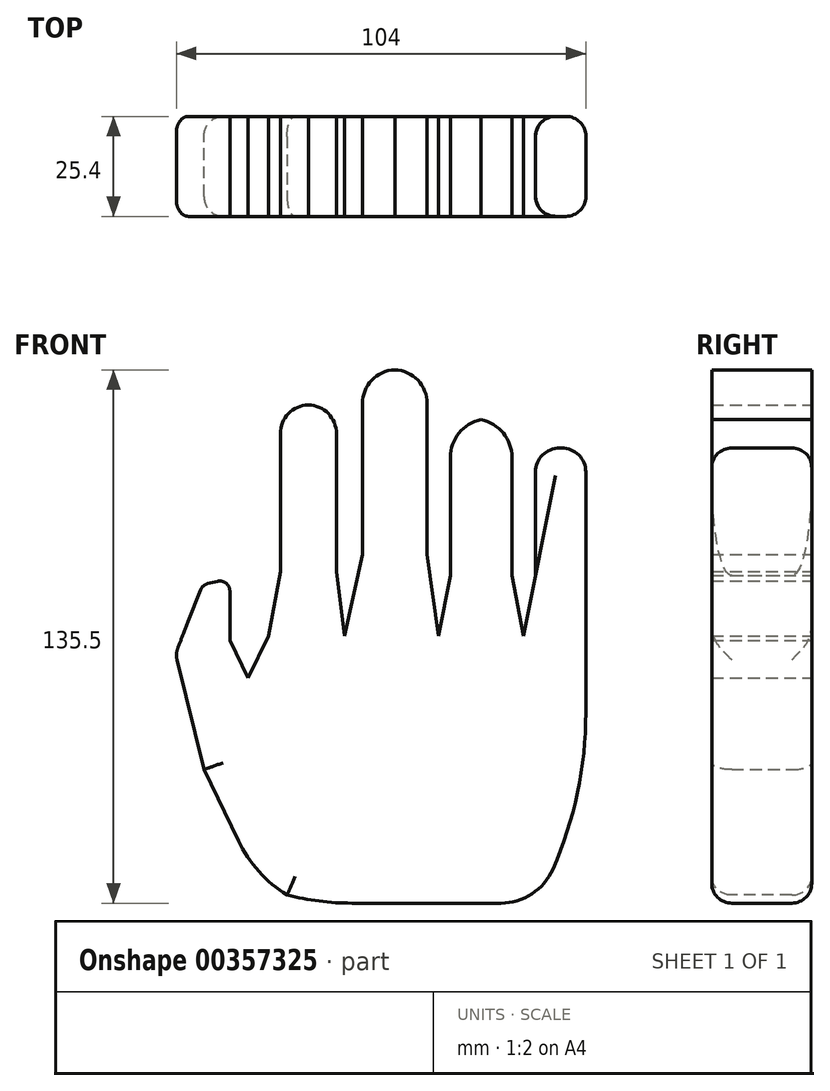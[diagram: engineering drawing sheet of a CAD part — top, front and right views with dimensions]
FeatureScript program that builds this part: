
annotation { "Feature Type Name" : "Feature", "Feature Type Description" : "" }
export const myFeature = defineFeature(function(context is Context, id is Id, definition is map)
    precondition{}
    {
        {
            var Q0;
            Q0=qCreatedBy(makeId("Front.planeOp"),FACE);
            var sketch = newSketch(context, id + "F0", { "sketchPlane" : qUnion([Q0])});
            skLineSegment(sketch, "E0.bottom", {"start": v(-40.3, 33.93) * mm, "end": v(40.3, 33.93) * mm});
            skLineSegment(sketch, "E0.top", {"start": v(-40.3, -33.93) * mm, "end": v(40.3, -33.93) * mm});
            skLineSegment(sketch, "E0.left", {"start": v(-40.3, 33.93) * mm, "end": v(-40.3, -33.93) * mm});
            skLineSegment(sketch, "E0.right", {"start": v(40.3, 33.93) * mm, "end": v(40.3, -33.93) * mm});
            skPoint(sketch, "E0.middle", {"position": v(0, 0) * mm});
            skLineSegment(sketch, "E1", {"start": v(-40.3, -33.93) * mm, "end": v(-56.71, 0) * mm});
            skLineSegment(sketch, "E2", {"start": v(-56.71, 0) * mm, "end": v(-40.3, 33.93) * mm});
            skLineSegment(sketch, "E3", {"start": v(-56.71, 0) * mm, "end": v(-63.94, 29.46) * mm});
            skLineSegment(sketch, "E4", {"start": v(-63.94, 29.46) * mm, "end": v(-50.13, 32.85) * mm});
            skLineSegment(sketch, "E5", {"start": v(-50.13, 32.85) * mm, "end": v(-45.48, 23.23) * mm});
            skLineSegment(sketch, "E6", {"start": v(-40.3, 33.93) * mm, "end": v(-37.32, 50.4) * mm});
            skLineSegment(sketch, "E7", {"start": v(-37.32, 50.4) * mm, "end": v(-23.05, 50.4) * mm});
            skLineSegment(sketch, "E8", {"start": v(-23.05, 50.4) * mm, "end": v(-23.05, 33.93) * mm});
            skLineSegment(sketch, "E9", {"start": v(-23.05, 33.93) * mm, "end": v(-16.47, 33.93) * mm});
            skLineSegment(sketch, "E10", {"start": v(-16.47, 33.93) * mm, "end": v(-16.47, 54.67) * mm});
            skLineSegment(sketch, "E11", {"start": v(-16.47, 54.67) * mm, "end": v(0, 54.67) * mm});
            skLineSegment(sketch, "E12", {"start": v(0, 54.67) * mm, "end": v(0, 33.93) * mm});
            skLineSegment(sketch, "E13", {"start": v(0, 33.93) * mm, "end": v(5.86, 33.93) * mm});
            skLineSegment(sketch, "E14", {"start": v(5.86, 33.93) * mm, "end": v(5.86, 49.26) * mm});
            skLineSegment(sketch, "E15", {"start": v(5.86, 49.26) * mm, "end": v(21.54, 49.26) * mm});
            skLineSegment(sketch, "E16", {"start": v(21.54, 49.26) * mm, "end": v(21.54, 33.93) * mm});
            skLineSegment(sketch, "E17", {"start": v(21.54, 33.93) * mm, "end": v(40.3, 33.93) * mm});
            skLineSegment(sketch, "E18", {"start": v(40.3, 49.26) * mm, "end": v(27.54, 49.26) * mm});
            skLineSegment(sketch, "E19", {"start": v(27.54, 49.26) * mm, "end": v(27.54, 33.93) * mm});
            skLineSegment(sketch, "E20", {"start": v(27.54, 33.93) * mm, "end": v(40.3, 33.93) * mm});
            skLineSegment(sketch, "E21", {"start": v(40.3, 33.93) * mm, "end": v(40.3, 49.26) * mm});
            skLineSegment(sketch, "E22", {"start": v(-37.32, 50.4) * mm, "end": v(-37.32, 70.26) * mm});
            skLineSegment(sketch, "E23", {"start": v(-37.32, 70.26) * mm, "end": v(-23.05, 70.26) * mm});
            skLineSegment(sketch, "E24", {"start": v(-23.05, 70.26) * mm, "end": v(-23.05, 50.4) * mm});
            skLineSegment(sketch, "E25", {"start": v(-16.47, 54.67) * mm, "end": v(-16.47, 76.1) * mm});
            skLineSegment(sketch, "E26", {"start": v(-16.47, 76.1) * mm, "end": v(0, 76.1) * mm});
            skLineSegment(sketch, "E27", {"start": v(0, 76.1) * mm, "end": v(0, 54.67) * mm});
            skLineSegment(sketch, "E28", {"start": v(5.86, 49.26) * mm, "end": v(5.86, 70.26) * mm});
            skLineSegment(sketch, "E29", {"start": v(5.86, 70.26) * mm, "end": v(21.54, 70.26) * mm});
            skLineSegment(sketch, "E30", {"start": v(21.54, 70.26) * mm, "end": v(21.54, 49.26) * mm});
            skLineSegment(sketch, "E31", {"start": v(27.54, 49.26) * mm, "end": v(27.54, 64.67) * mm});
            skLineSegment(sketch, "E32", {"start": v(27.54, 64.67) * mm, "end": v(40.3, 64.67) * mm});
            skLineSegment(sketch, "E33", {"start": v(40.3, 64.67) * mm, "end": v(40.3, 49.26) * mm});
            skLineSegment(sketch, "E34", {"start": v(-37.32, 70.26) * mm, "end": v(-37.32, 92.7) * mm});
            skLineSegment(sketch, "E35", {"start": v(-37.32, 92.7) * mm, "end": v(-23.05, 92.7) * mm});
            skLineSegment(sketch, "E36", {"start": v(-23.05, 92.7) * mm, "end": v(-23.05, 70.26) * mm});
            skLineSegment(sketch, "E37", {"start": v(-16.47, 76.1) * mm, "end": v(-16.47, 101.57) * mm});
            skLineSegment(sketch, "E38", {"start": v(-16.47, 101.57) * mm, "end": v(0, 101.57) * mm});
            skLineSegment(sketch, "E39", {"start": v(0, 101.57) * mm, "end": v(0, 76.1) * mm});
            skLineSegment(sketch, "E40", {"start": v(5.86, 70.26) * mm, "end": v(5.86, 89.12) * mm});
            skLineSegment(sketch, "E41", {"start": v(5.86, 89.12) * mm, "end": v(21.54, 89.12) * mm});
            skLineSegment(sketch, "E42", {"start": v(21.54, 89.12) * mm, "end": v(21.54, 70.26) * mm});
            skLineSegment(sketch, "E43", {"start": v(27.54, 64.67) * mm, "end": v(27.54, 81.74) * mm});
            skLineSegment(sketch, "E44", {"start": v(27.54, 81.74) * mm, "end": v(40.3, 81.74) * mm});
            skLineSegment(sketch, "E45", {"start": v(40.3, 81.74) * mm, "end": v(40.3, 64.67) * mm});
            skLineSegment(sketch, "E46", {"start": v(-63.94, 29.46) * mm, "end": v(-57.03, 46.92) * mm});
            skPoint(sketch, "E46.endSnap0", {"position": v(-57.03, 31.16) * mm});
            skLineSegment(sketch, "E47", {"start": v(-57.03, 46.92) * mm, "end": v(-50.13, 48.6) * mm});
            skLineSegment(sketch, "E48", {"start": v(-50.13, 48.6) * mm, "end": v(-50.13, 32.85) * mm});
            skPoint(sketch, "E49", {"position": v(-40.3, 0) * mm});
            skLineSegment(sketch, "E50", {"start": v(-23.05, 50.4) * mm, "end": v(-20.99, 33.93) * mm});
            skLineSegment(sketch, "E51", {"start": v(-20.99, 33.93) * mm, "end": v(-16.47, 54.67) * mm});
            skLineSegment(sketch, "E52", {"start": v(0, 54.67) * mm, "end": v(2.93, 33.93) * mm});
            skLineSegment(sketch, "E53", {"start": v(2.93, 33.93) * mm, "end": v(5.86, 49.26) * mm});
            skLineSegment(sketch, "E54", {"start": v(21.54, 49.26) * mm, "end": v(24.49, 33.93) * mm});
            skLineSegment(sketch, "E55", {"start": v(24.49, 33.93) * mm, "end": v(27.54, 49.26) * mm});
            skSolve(sketch);
        }
        {
            var Q0;
            Q0 = qSketchRegion(id + "F0", true);
            extrude(context, id + "F1", {"entities" : qUnion([Q0]), "endBound" : BoundingType.SYMMETRIC, "depth" : 25.4 * mm});
        }
        {
            var Q0;
            Q0=makeQuery(id+"F1.opExtrude","SWEPT_EDGE",EDGE,{"disambiguationData":[OSD([sQuery(id+"F0.wireOp",EDGE,"E0.top"),sQuery(id+"F0.wireOp",EDGE,"E0.right")])]});
            var Q1;
            Q1=makeQuery(id+"F1.opExtrude","SWEPT_EDGE",EDGE,{"disambiguationData":[OSD([sQuery(id+"F0.wireOp",EDGE,"E0.top"),sQuery(id+"F0.wireOp",EDGE,"E0.left"),sQuery(id+"F0.wireOp",EDGE,"E1")])]});
            chamfer(context, id + "F2", {"entities" : qUnion([Q0, Q1]), "width" : 12.7 * mm, "tangentPropagation" : true});
        }
        {
            var Q0;
            {var subQ0=sQuery(id+"F0.wireOp",EDGE,"E0.right");Q0=makeQuery(id+"F2.opChamfer","BLEND_EDGE",EDGE,{"blendedFrom":[makeQuery(id+"F1.opExtrude","SWEPT_EDGE",EDGE,{"disambiguationData":[OSD([sQuery(id+"F0.wireOp",EDGE,"E0.top"),subQ0])]}),makeQuery(id+"F1.opExtrude","SWEPT_FACE",FACE,{"disambiguationData":[OSD([subQ0,sQuery(id+"F0.wireOp",EDGE,"E21"),sQuery(id+"F0.wireOp",EDGE,"E33"),sQuery(id+"F0.wireOp",EDGE,"E45")])]})],"blendedInto":[makeQuery(id+"F1.opExtrude","SWEPT_FACE",FACE,{"disambiguationData":[OSD([subQ0,sQuery(id+"F0.wireOp",EDGE,"E21"),sQuery(id+"F0.wireOp",EDGE,"E33"),sQuery(id+"F0.wireOp",EDGE,"E45")])]})]});}
            fillet(context, id + "F3", {"entities" : qUnion([Q0]), "radius" : 98.65 * mm, "tangentPropagation" : true, "allowEdgeOverflow" : false});
        }
        {
            var Q0;
            {var subQ0=sQuery(id+"F0.wireOp",EDGE,"E0.top");var subQ1=sQuery(id+"F0.wireOp",EDGE,"E0.right");Q0=makeQuery(id+"F3.opFillet","BLEND_EDGE",EDGE,{"blendedFrom":[makeQuery(id+"F2.opChamfer","BLEND_EDGE",EDGE,{"blendedFrom":[makeQuery(id+"F1.opExtrude","SWEPT_EDGE",EDGE,{"disambiguationData":[OSD([subQ0,subQ1])]}),makeQuery(id+"F1.opExtrude","SWEPT_FACE",FACE,{"disambiguationData":[OSD([subQ1,sQuery(id+"F0.wireOp",EDGE,"E21"),sQuery(id+"F0.wireOp",EDGE,"E33"),sQuery(id+"F0.wireOp",EDGE,"E45")])]})],"blendedInto":[makeQuery(id+"F1.opExtrude","SWEPT_FACE",FACE,{"disambiguationData":[OSD([subQ1,sQuery(id+"F0.wireOp",EDGE,"E21"),sQuery(id+"F0.wireOp",EDGE,"E33"),sQuery(id+"F0.wireOp",EDGE,"E45")])]})]}),makeQuery(id+"F1.opExtrude","SWEPT_FACE",FACE,{"disambiguationData":[OSD([subQ0])]})],"blendedInto":[makeQuery(id+"F1.opExtrude","SWEPT_FACE",FACE,{"disambiguationData":[OSD([subQ0])]})]});}
            fillet(context, id + "F4", {"entities" : qUnion([Q0]), "radius" : 14.45 * mm, "tangentPropagation" : true, "allowEdgeOverflow" : false});
        }
        {
            var Q0;
            {var subQ0=sQuery(id+"F0.wireOp",EDGE,"E1");Q0=makeQuery(id+"F2.opChamfer","BLEND_EDGE",EDGE,{"blendedFrom":[makeQuery(id+"F1.opExtrude","SWEPT_EDGE",EDGE,{"disambiguationData":[OSD([sQuery(id+"F0.wireOp",EDGE,"E0.top"),sQuery(id+"F0.wireOp",EDGE,"E0.left"),subQ0])]}),makeQuery(id+"F1.opExtrude","SWEPT_FACE",FACE,{"disambiguationData":[OSD([subQ0])]})],"blendedInto":[makeQuery(id+"F1.opExtrude","SWEPT_FACE",FACE,{"disambiguationData":[OSD([subQ0])]})]});}
            fillet(context, id + "F5", {"entities" : qUnion([Q0]), "radius" : 33.5 * mm, "tangentPropagation" : true, "allowEdgeOverflow" : false});
        }
        {
            var Q0;
            {var subQ0=sQuery(id+"F0.wireOp",EDGE,"E0.top");Q0=makeQuery(id+"F2.opChamfer","BLEND_EDGE",EDGE,{"blendedFrom":[makeQuery(id+"F1.opExtrude","SWEPT_EDGE",EDGE,{"disambiguationData":[OSD([subQ0,sQuery(id+"F0.wireOp",EDGE,"E0.left"),sQuery(id+"F0.wireOp",EDGE,"E1")])]}),makeQuery(id+"F1.opExtrude","SWEPT_FACE",FACE,{"disambiguationData":[OSD([subQ0])]})],"blendedInto":[makeQuery(id+"F1.opExtrude","SWEPT_FACE",FACE,{"disambiguationData":[OSD([subQ0])]})]});}
            fillet(context, id + "F6", {"entities" : qUnion([Q0]), "radius" : 67 * mm, "tangentPropagation" : true, "allowEdgeOverflow" : false});
        }
        {
            var Q0;
            Q0=makeQuery(id+"F1.opExtrude","SWEPT_EDGE",EDGE,{"disambiguationData":[OSD([sQuery(id+"F0.wireOp",EDGE,"E46"),sQuery(id+"F0.wireOp",EDGE,"E47")])]});
            var Q1;
            Q1=makeQuery(id+"F1.opExtrude","SWEPT_EDGE",EDGE,{"disambiguationData":[OSD([sQuery(id+"F0.wireOp",EDGE,"E47"),sQuery(id+"F0.wireOp",EDGE,"E48")])]});
            fillet(context, id + "F7", {"entities" : qUnion([Q0, Q1]), "radius" : 2.54 * mm, "tangentPropagation" : true, "allowEdgeOverflow" : false});
        }
        {
            var Q0;
            Q0=makeQuery(id+"F1.opExtrude","SWEPT_EDGE",EDGE,{"disambiguationData":[OSD([sQuery(id+"F0.wireOp",EDGE,"E34"),sQuery(id+"F0.wireOp",EDGE,"E35")])]});
            var Q1;
            Q1=makeQuery(id+"F1.opExtrude","SWEPT_EDGE",EDGE,{"disambiguationData":[OSD([sQuery(id+"F0.wireOp",EDGE,"E35"),sQuery(id+"F0.wireOp",EDGE,"E36")])]});
            fillet(context, id + "F8", {"entities" : qUnion([Q0, Q1]), "radius" : 7.36 * mm, "tangentPropagation" : true, "allowEdgeOverflow" : false});
        }
        {
            var Q0;
            Q0=makeQuery(id+"F1.opExtrude","SWEPT_EDGE",EDGE,{"disambiguationData":[OSD([sQuery(id+"F0.wireOp",EDGE,"E37"),sQuery(id+"F0.wireOp",EDGE,"E38")])]});
            var Q1;
            Q1=makeQuery(id+"F1.opExtrude","SWEPT_EDGE",EDGE,{"disambiguationData":[OSD([sQuery(id+"F0.wireOp",EDGE,"E38"),sQuery(id+"F0.wireOp",EDGE,"E39")])]});
            fillet(context, id + "F9", {"entities" : qUnion([Q0, Q1]), "radius" : 8.58 * mm, "tangentPropagation" : true, "allowEdgeOverflow" : false});
        }
        {
            var Q0;
            Q0=makeQuery(id+"F1.opExtrude","SWEPT_EDGE",EDGE,{"disambiguationData":[OSD([sQuery(id+"F0.wireOp",EDGE,"E40"),sQuery(id+"F0.wireOp",EDGE,"E41")])]});
            var Q1;
            Q1=makeQuery(id+"F1.opExtrude","SWEPT_EDGE",EDGE,{"disambiguationData":[OSD([sQuery(id+"F0.wireOp",EDGE,"E41"),sQuery(id+"F0.wireOp",EDGE,"E42")])]});
            fillet(context, id + "F10", {"entities" : qUnion([Q0, Q1]), "radius" : 9.8 * mm, "tangentPropagation" : true, "allowEdgeOverflow" : false});
        }
        {
            var Q0;
            Q0=makeQuery(id+"F1.opExtrude","SWEPT_EDGE",EDGE,{"disambiguationData":[OSD([sQuery(id+"F0.wireOp",EDGE,"E44"),sQuery(id+"F0.wireOp",EDGE,"E45")])]});
            var Q1;
            Q1=makeQuery(id+"F1.opExtrude","SWEPT_EDGE",EDGE,{"disambiguationData":[OSD([sQuery(id+"F0.wireOp",EDGE,"E43"),sQuery(id+"F0.wireOp",EDGE,"E44")])]});
            fillet(context, id + "F11", {"entities" : qUnion([Q0, Q1]), "radius" : 6.13 * mm, "tangentPropagation" : true, "allowEdgeOverflow" : false});
        }
        {
            var Q0;
            {var subQ0=sQuery(id+"F0.wireOp",EDGE,"E45");var subQ1=sQuery(id+"F0.wireOp",EDGE,"E33");var subQ2=sQuery(id+"F0.wireOp",EDGE,"E21");var subQ3=sQuery(id+"F0.wireOp",EDGE,"E0.right");var subQ4=sQuery(id+"F0.wireOp",EDGE,"E0.top");Q0=makeQuery(id+"F3.opFillet","BLEND_EDGE",EDGE,{"blendedFrom":[makeQuery(id+"F2.opChamfer","BLEND_EDGE",EDGE,{"blendedFrom":[makeQuery(id+"F1.opExtrude","SWEPT_EDGE",EDGE,{"disambiguationData":[OSD([subQ4,subQ3])]}),makeQuery(id+"F1.opExtrude","SWEPT_FACE",FACE,{"disambiguationData":[OSD([subQ3,subQ2,subQ1,subQ0])]})],"blendedInto":[makeQuery(id+"F1.opExtrude","SWEPT_FACE",FACE,{"disambiguationData":[OSD([subQ3,subQ2,subQ1,subQ0])]})]}),makeQuery(id+"F1.opExtrude","CAP_FACE",FACE,{"disambiguationData":[OSD([subQ4,subQ3,sQuery(id+"F0.wireOp",EDGE,"E1"),sQuery(id+"F0.wireOp",EDGE,"E2"),sQuery(id+"F0.wireOp",EDGE,"E3"),sQuery(id+"F0.wireOp",EDGE,"E5"),sQuery(id+"F0.wireOp",EDGE,"E6"),subQ2,sQuery(id+"F0.wireOp",EDGE,"E22"),sQuery(id+"F0.wireOp",EDGE,"E24"),sQuery(id+"F0.wireOp",EDGE,"E25"),sQuery(id+"F0.wireOp",EDGE,"E27"),sQuery(id+"F0.wireOp",EDGE,"E28"),sQuery(id+"F0.wireOp",EDGE,"E30"),sQuery(id+"F0.wireOp",EDGE,"E31"),subQ1,sQuery(id+"F0.wireOp",EDGE,"E34"),sQuery(id+"F0.wireOp",EDGE,"E35"),sQuery(id+"F0.wireOp",EDGE,"E36"),sQuery(id+"F0.wireOp",EDGE,"E37"),sQuery(id+"F0.wireOp",EDGE,"E38"),sQuery(id+"F0.wireOp",EDGE,"E39"),sQuery(id+"F0.wireOp",EDGE,"E40"),sQuery(id+"F0.wireOp",EDGE,"E41"),sQuery(id+"F0.wireOp",EDGE,"E42"),sQuery(id+"F0.wireOp",EDGE,"E43"),sQuery(id+"F0.wireOp",EDGE,"E44"),subQ0,sQuery(id+"F0.wireOp",EDGE,"E46"),sQuery(id+"F0.wireOp",EDGE,"E47"),sQuery(id+"F0.wireOp",EDGE,"E48"),sQuery(id+"F0.wireOp",EDGE,"E50"),sQuery(id+"F0.wireOp",EDGE,"E51"),sQuery(id+"F0.wireOp",EDGE,"E52"),sQuery(id+"F0.wireOp",EDGE,"E53"),sQuery(id+"F0.wireOp",EDGE,"E54"),sQuery(id+"F0.wireOp",EDGE,"E55")])],"isStart":true})],"blendedInto":[makeQuery(id+"F1.opExtrude","CAP_FACE",FACE,{"disambiguationData":[OSD([subQ4,subQ3,sQuery(id+"F0.wireOp",EDGE,"E1"),sQuery(id+"F0.wireOp",EDGE,"E2"),sQuery(id+"F0.wireOp",EDGE,"E3"),sQuery(id+"F0.wireOp",EDGE,"E5"),sQuery(id+"F0.wireOp",EDGE,"E6"),subQ2,sQuery(id+"F0.wireOp",EDGE,"E22"),sQuery(id+"F0.wireOp",EDGE,"E24"),sQuery(id+"F0.wireOp",EDGE,"E25"),sQuery(id+"F0.wireOp",EDGE,"E27"),sQuery(id+"F0.wireOp",EDGE,"E28"),sQuery(id+"F0.wireOp",EDGE,"E30"),sQuery(id+"F0.wireOp",EDGE,"E31"),subQ1,sQuery(id+"F0.wireOp",EDGE,"E34"),sQuery(id+"F0.wireOp",EDGE,"E35"),sQuery(id+"F0.wireOp",EDGE,"E36"),sQuery(id+"F0.wireOp",EDGE,"E37"),sQuery(id+"F0.wireOp",EDGE,"E38"),sQuery(id+"F0.wireOp",EDGE,"E39"),sQuery(id+"F0.wireOp",EDGE,"E40"),sQuery(id+"F0.wireOp",EDGE,"E41"),sQuery(id+"F0.wireOp",EDGE,"E42"),sQuery(id+"F0.wireOp",EDGE,"E43"),sQuery(id+"F0.wireOp",EDGE,"E44"),subQ0,sQuery(id+"F0.wireOp",EDGE,"E46"),sQuery(id+"F0.wireOp",EDGE,"E47"),sQuery(id+"F0.wireOp",EDGE,"E48"),sQuery(id+"F0.wireOp",EDGE,"E50"),sQuery(id+"F0.wireOp",EDGE,"E51"),sQuery(id+"F0.wireOp",EDGE,"E52"),sQuery(id+"F0.wireOp",EDGE,"E53"),sQuery(id+"F0.wireOp",EDGE,"E54"),sQuery(id+"F0.wireOp",EDGE,"E55")])],"isStart":true})]});}
            var Q1;
            Q1=makeQuery(id+"F1.opExtrude","CAP_EDGE",EDGE,{"disambiguationData":[OSD([sQuery(id+"F0.wireOp",EDGE,"E1")])],"isStart":true});
            var Q2;
            Q2=makeQuery(id+"F1.opExtrude","CAP_EDGE",EDGE,{"disambiguationData":[OSD([sQuery(id+"F0.wireOp",EDGE,"E3")])],"isStart":true});
            var Q3;
            {var subQ0=sQuery(id+"F0.wireOp",EDGE,"E45");var subQ1=sQuery(id+"F0.wireOp",EDGE,"E33");var subQ2=sQuery(id+"F0.wireOp",EDGE,"E21");var subQ3=sQuery(id+"F0.wireOp",EDGE,"E0.right");var subQ4=sQuery(id+"F0.wireOp",EDGE,"E0.top");Q3=makeQuery(id+"F3.opFillet","BLEND_EDGE",EDGE,{"blendedFrom":[makeQuery(id+"F2.opChamfer","BLEND_EDGE",EDGE,{"blendedFrom":[makeQuery(id+"F1.opExtrude","SWEPT_EDGE",EDGE,{"disambiguationData":[OSD([subQ4,subQ3])]}),makeQuery(id+"F1.opExtrude","SWEPT_FACE",FACE,{"disambiguationData":[OSD([subQ3,subQ2,subQ1,subQ0])]})],"blendedInto":[makeQuery(id+"F1.opExtrude","SWEPT_FACE",FACE,{"disambiguationData":[OSD([subQ3,subQ2,subQ1,subQ0])]})]}),makeQuery(id+"F1.opExtrude","CAP_FACE",FACE,{"disambiguationData":[OSD([subQ4,subQ3,sQuery(id+"F0.wireOp",EDGE,"E1"),sQuery(id+"F0.wireOp",EDGE,"E2"),sQuery(id+"F0.wireOp",EDGE,"E3"),sQuery(id+"F0.wireOp",EDGE,"E5"),sQuery(id+"F0.wireOp",EDGE,"E6"),subQ2,sQuery(id+"F0.wireOp",EDGE,"E22"),sQuery(id+"F0.wireOp",EDGE,"E24"),sQuery(id+"F0.wireOp",EDGE,"E25"),sQuery(id+"F0.wireOp",EDGE,"E27"),sQuery(id+"F0.wireOp",EDGE,"E28"),sQuery(id+"F0.wireOp",EDGE,"E30"),sQuery(id+"F0.wireOp",EDGE,"E31"),subQ1,sQuery(id+"F0.wireOp",EDGE,"E34"),sQuery(id+"F0.wireOp",EDGE,"E35"),sQuery(id+"F0.wireOp",EDGE,"E36"),sQuery(id+"F0.wireOp",EDGE,"E37"),sQuery(id+"F0.wireOp",EDGE,"E38"),sQuery(id+"F0.wireOp",EDGE,"E39"),sQuery(id+"F0.wireOp",EDGE,"E40"),sQuery(id+"F0.wireOp",EDGE,"E41"),sQuery(id+"F0.wireOp",EDGE,"E42"),sQuery(id+"F0.wireOp",EDGE,"E43"),sQuery(id+"F0.wireOp",EDGE,"E44"),subQ0,sQuery(id+"F0.wireOp",EDGE,"E46"),sQuery(id+"F0.wireOp",EDGE,"E47"),sQuery(id+"F0.wireOp",EDGE,"E48"),sQuery(id+"F0.wireOp",EDGE,"E50"),sQuery(id+"F0.wireOp",EDGE,"E51"),sQuery(id+"F0.wireOp",EDGE,"E52"),sQuery(id+"F0.wireOp",EDGE,"E53"),sQuery(id+"F0.wireOp",EDGE,"E54"),sQuery(id+"F0.wireOp",EDGE,"E55")])],"isStart":false})],"blendedInto":[makeQuery(id+"F1.opExtrude","CAP_FACE",FACE,{"disambiguationData":[OSD([subQ4,subQ3,sQuery(id+"F0.wireOp",EDGE,"E1"),sQuery(id+"F0.wireOp",EDGE,"E2"),sQuery(id+"F0.wireOp",EDGE,"E3"),sQuery(id+"F0.wireOp",EDGE,"E5"),sQuery(id+"F0.wireOp",EDGE,"E6"),subQ2,sQuery(id+"F0.wireOp",EDGE,"E22"),sQuery(id+"F0.wireOp",EDGE,"E24"),sQuery(id+"F0.wireOp",EDGE,"E25"),sQuery(id+"F0.wireOp",EDGE,"E27"),sQuery(id+"F0.wireOp",EDGE,"E28"),sQuery(id+"F0.wireOp",EDGE,"E30"),sQuery(id+"F0.wireOp",EDGE,"E31"),subQ1,sQuery(id+"F0.wireOp",EDGE,"E34"),sQuery(id+"F0.wireOp",EDGE,"E35"),sQuery(id+"F0.wireOp",EDGE,"E36"),sQuery(id+"F0.wireOp",EDGE,"E37"),sQuery(id+"F0.wireOp",EDGE,"E38"),sQuery(id+"F0.wireOp",EDGE,"E39"),sQuery(id+"F0.wireOp",EDGE,"E40"),sQuery(id+"F0.wireOp",EDGE,"E41"),sQuery(id+"F0.wireOp",EDGE,"E42"),sQuery(id+"F0.wireOp",EDGE,"E43"),sQuery(id+"F0.wireOp",EDGE,"E44"),subQ0,sQuery(id+"F0.wireOp",EDGE,"E46"),sQuery(id+"F0.wireOp",EDGE,"E47"),sQuery(id+"F0.wireOp",EDGE,"E48"),sQuery(id+"F0.wireOp",EDGE,"E50"),sQuery(id+"F0.wireOp",EDGE,"E51"),sQuery(id+"F0.wireOp",EDGE,"E52"),sQuery(id+"F0.wireOp",EDGE,"E53"),sQuery(id+"F0.wireOp",EDGE,"E54"),sQuery(id+"F0.wireOp",EDGE,"E55")])],"isStart":false})]});}
            var Q4;
            Q4=makeQuery(id+"F1.opExtrude","CAP_EDGE",EDGE,{"disambiguationData":[OSD([sQuery(id+"F0.wireOp",EDGE,"E1")])],"isStart":false});
            var Q5;
            Q5=makeQuery(id+"F1.opExtrude","CAP_EDGE",EDGE,{"disambiguationData":[OSD([sQuery(id+"F0.wireOp",EDGE,"E3")])],"isStart":false});
            var Q6;
            Q6=makeQuery(id+"F1.opExtrude","SWEPT_EDGE",EDGE,{"disambiguationData":[OSD([sQuery(id+"F0.wireOp",EDGE,"E3"),sQuery(id+"F0.wireOp",EDGE,"E4"),sQuery(id+"F0.wireOp",EDGE,"E46")])]});
            fillet(context, id + "F12", {"entities" : qUnion([Q0, Q1, Q2, Q3, Q4, Q5, Q6]), "radius" : 5.08 * mm, "tangentPropagation" : true, "allowEdgeOverflow" : false});
        }
    });
